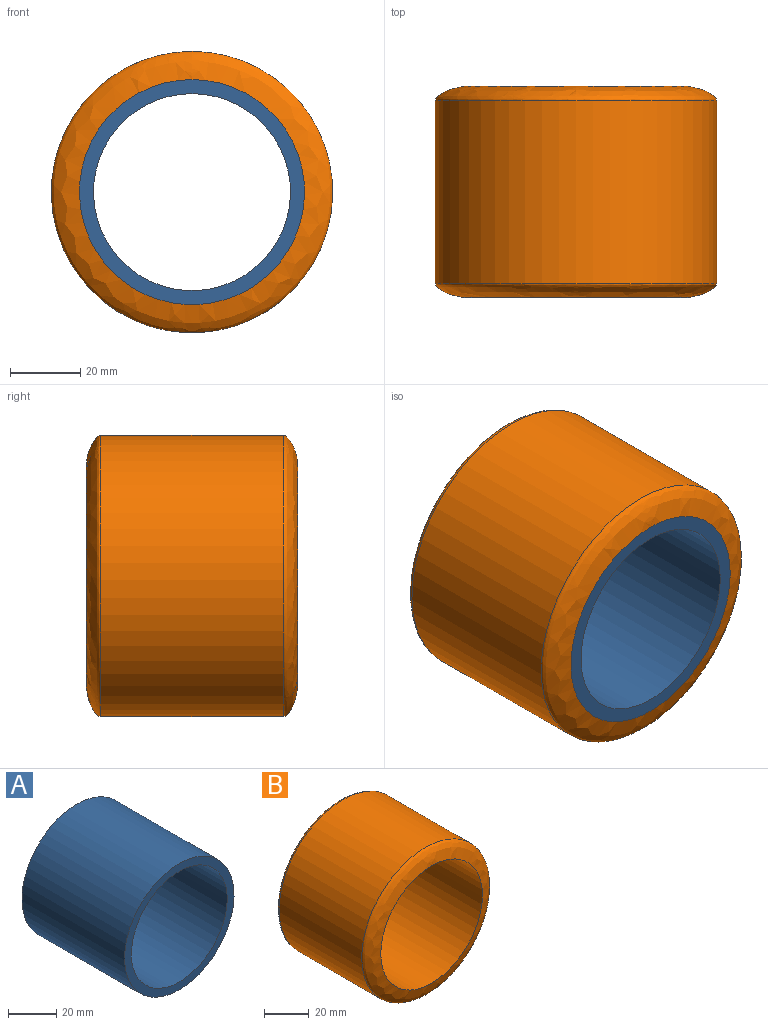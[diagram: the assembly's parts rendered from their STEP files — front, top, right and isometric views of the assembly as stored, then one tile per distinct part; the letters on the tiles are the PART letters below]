
ASSEMBLY  parts=2 mates=1
PART A: 4 faces, bbox 64x60x64 mm
  f0: plane 64x64mm, normal (0,1,0), area 754mm2, adj f1,f3
  f1: cylinder r=32mm len=64mm, axis (0,1,0), area 12063.7mm2, adj f0,f2
  f2: plane 64x64mm, normal (0,-1,0), area 754mm2, adj f1,f3
  f3: cylinder r=28mm len=60mm, axis (0,1,0), area 10555.8mm2, adj f0,f2
PART B: 4 faces, bbox 160x60x80 mm
  f0: cylinder r=32mm len=64mm, axis (0,1,0), area 12063.7mm2, adj f1,f2
  f1: bspline ~160x80mm, area 2144.6mm2, adj f0,f3
  f2: bspline ~160x80mm, area 2144.6mm2, adj f0,f3
  f3: cylinder r=40mm len=80mm, axis (0,1,0), area 13069mm2, adj f1,f2
PLACE A t=(47.3,132,72.5)mm
PLACE B t=(47.3,132,72.5)mm fixed
MATE fastened A.f1 <-> B.f3  axis (0,1,0) through (47.3,162,72.5)mm
